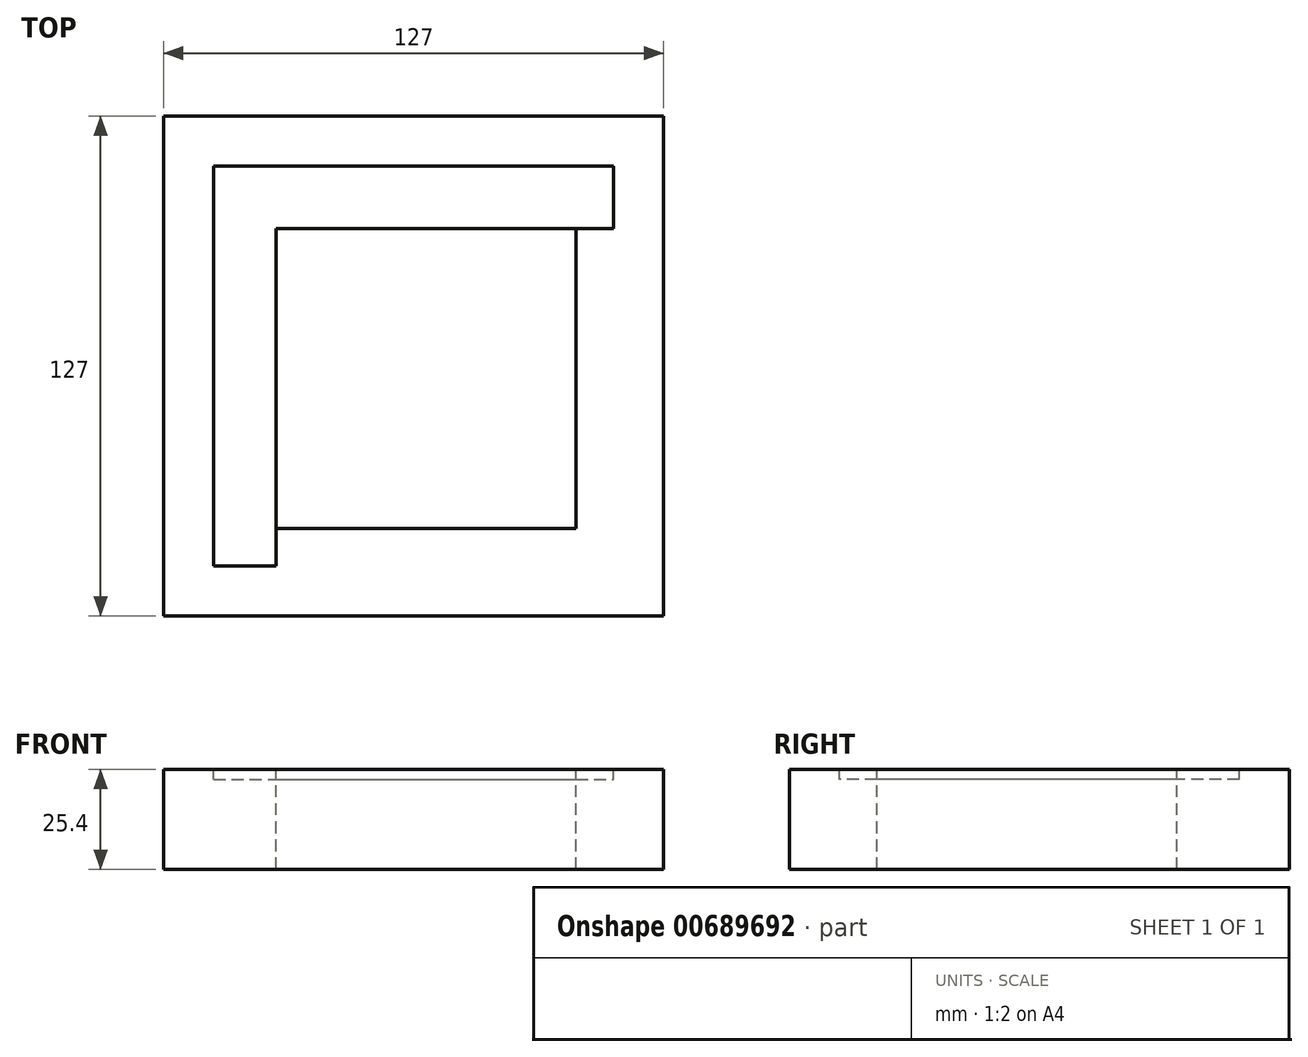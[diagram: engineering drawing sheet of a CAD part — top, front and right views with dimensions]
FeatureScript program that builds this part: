
annotation { "Feature Type Name" : "Feature", "Feature Type Description" : "" }
export const myFeature = defineFeature(function(context is Context, id is Id, definition is map)
    precondition{}
    {
        {
            var Q0;
            Q0=qCreatedBy(makeId("Top.planeOp"),FACE);
            var sketch = newSketch(context, id + "F0", { "sketchPlane" : qUnion([Q0])});
            skLineSegment(sketch, "E0.bottom", {"start": v(-63.5, 63.5) * mm, "end": v(63.5, 63.5) * mm});
            skLineSegment(sketch, "E0.top", {"start": v(-63.5, -63.5) * mm, "end": v(63.5, -63.5) * mm});
            skLineSegment(sketch, "E0.left", {"start": v(-63.5, 63.5) * mm, "end": v(-63.5, -63.5) * mm});
            skLineSegment(sketch, "E0.right", {"start": v(63.5, 63.5) * mm, "end": v(63.5, -63.5) * mm});
            skPoint(sketch, "E0.middle", {"position": v(0, 0) * mm});
            skLineSegment(sketch, "E1.bottom", {"start": v(-50.8, 34.93) * mm, "end": v(-34.92, 34.93) * mm});
            skLineSegment(sketch, "E1.top", {"start": v(-50.8, -50.8) * mm, "end": v(-34.92, -50.8) * mm});
            skLineSegment(sketch, "E1.left", {"start": v(-50.8, 34.92) * mm, "end": v(-50.8, -50.8) * mm});
            skLineSegment(sketch, "E1.right", {"start": v(-34.92, 34.92) * mm, "end": v(-34.92, -50.8) * mm});
            skPoint(sketch, "E2.oppositeSnap0", {"position": v(-42.86, 34.92) * mm});
            skLineSegment(sketch, "E2.bottom", {"start": v(-50.8, 50.8) * mm, "end": v(50.8, 50.8) * mm});
            skLineSegment(sketch, "E2.top", {"start": v(-50.8, 34.93) * mm, "end": v(50.8, 34.93) * mm});
            skLineSegment(sketch, "E2.left", {"start": v(-50.8, 50.8) * mm, "end": v(-50.8, 34.92) * mm});
            skLineSegment(sketch, "E2.right", {"start": v(50.8, 50.8) * mm, "end": v(50.8, 34.93) * mm});
            skLineSegment(sketch, "E3.bottom", {"start": v(-34.92, 34.93) * mm, "end": v(41.28, 34.93) * mm});
            skLineSegment(sketch, "E3.top", {"start": v(-34.92, -41.28) * mm, "end": v(41.28, -41.28) * mm});
            skLineSegment(sketch, "E3.left", {"start": v(-34.92, 34.92) * mm, "end": v(-34.92, -41.28) * mm});
            skLineSegment(sketch, "E3.right", {"start": v(41.27, 34.92) * mm, "end": v(41.27, -41.28) * mm});
            skLineSegment(sketch, "E4", {"start": v(-42.86, -50.8) * mm, "end": v(-42.86, 42.86) * mm, "construction": true});
            skLineSegment(sketch, "E5", {"start": v(-42.86, 42.86) * mm, "end": v(50.8, 42.86) * mm, "construction": true});
            skPoint(sketch, "E6", {"position": v(22.23, -25.21) * mm});
            skPoint(sketch, "E7", {"position": v(-15.87, -25.21) * mm});
            skPoint(sketch, "E8", {"position": v(-15.87, 15.87) * mm});
            skPoint(sketch, "E9", {"position": v(22.23, 15.87) * mm});
            skSolve(sketch);
        }
        {
            var Q0;
            Q0=makeQuery(id+"F0.imprint","IMPRINT",FACE,{"disambiguationData":[TD([[makeQuery(id+"F0.imprint","IMPRINT",EDGE,{"derivedFrom":sQuery(id+"F0.wireOp",EDGE,"E0.bottom")}),-1.0]])]});
            var Q1;
            Q1=makeQuery(id+"F0.imprint","IMPRINT",FACE,{"disambiguationData":[TD([[makeQuery(id+"F0.imprint","IMPRINT",EDGE,{"derivedFrom":sQuery(id+"F0.wireOp",EDGE,"E3.bottom")}),-1.0]])]});
            var Q2;
            Q2=makeQuery(id+"F0.imprint","IMPRINT",FACE,{"disambiguationData":[TD([[makeQuery(id+"F0.imprint","IMPRINT",EDGE,{"derivedFrom":sQuery(id+"F0.wireOp",EDGE,"E1.top")}),1.0]])]});
            var Q3;
            Q3=makeQuery(id+"F0.imprint","IMPRINT",FACE,{"disambiguationData":[TD([[makeQuery(id+"F0.imprint","IMPRINT",EDGE,{"derivedFrom":sQuery(id+"F0.wireOp",EDGE,"E2.bottom")}),-1.0]])]});
            var Q4;
            Q4=sQuery(id+"F0.wireOp",EDGE,"E0.left");
            var Q5;
            Q5=sQuery(id+"F0.wireOp",EDGE,"E0.top");
            var Q6;
            Q6=sQuery(id+"F0.wireOp",EDGE,"E0.right");
            var Q7;
            Q7=sQuery(id+"F0.wireOp",EDGE,"E0.bottom");
            extrude(context, id + "F1", {"entities" : qUnion([Q0, Q1, Q2, Q3]), "surfaceEntities" : qUnion([Q4, Q5, Q6, Q7]), "oppositeDirection" : true, "depth" : 25.4 * mm, "offsetDistance" : 25.4 * mm});
        }
        {
            var Q0;
            Q0=makeQuery(id+"F0.imprint","IMPRINT",FACE,{"disambiguationData":[TD([[makeQuery(id+"F0.imprint","IMPRINT",EDGE,{"derivedFrom":sQuery(id+"F0.wireOp",EDGE,"E1.top")}),1.0]])]});
            var Q1;
            Q1=makeQuery(id+"F0.imprint","IMPRINT",FACE,{"disambiguationData":[TD([[makeQuery(id+"F0.imprint","IMPRINT",EDGE,{"derivedFrom":sQuery(id+"F0.wireOp",EDGE,"E2.bottom")}),-1.0]])]});
            var Q2;
            Q2=makeQuery(id+"F0.imprint","IMPRINT",FACE,{"disambiguationData":[TD([[makeQuery(id+"F0.imprint","IMPRINT",EDGE,{"derivedFrom":sQuery(id+"F0.wireOp",EDGE,"E3.bottom")}),-1.0]])]});
            extrude(context, id + "F2", {"entities" : qUnion([Q0, Q1, Q2]), "operationType" : NewBodyOperationType.REMOVE, "oppositeDirection" : true, "depth" : 2.54 * mm, "offsetDistance" : 25.4 * mm});
        }
    });
